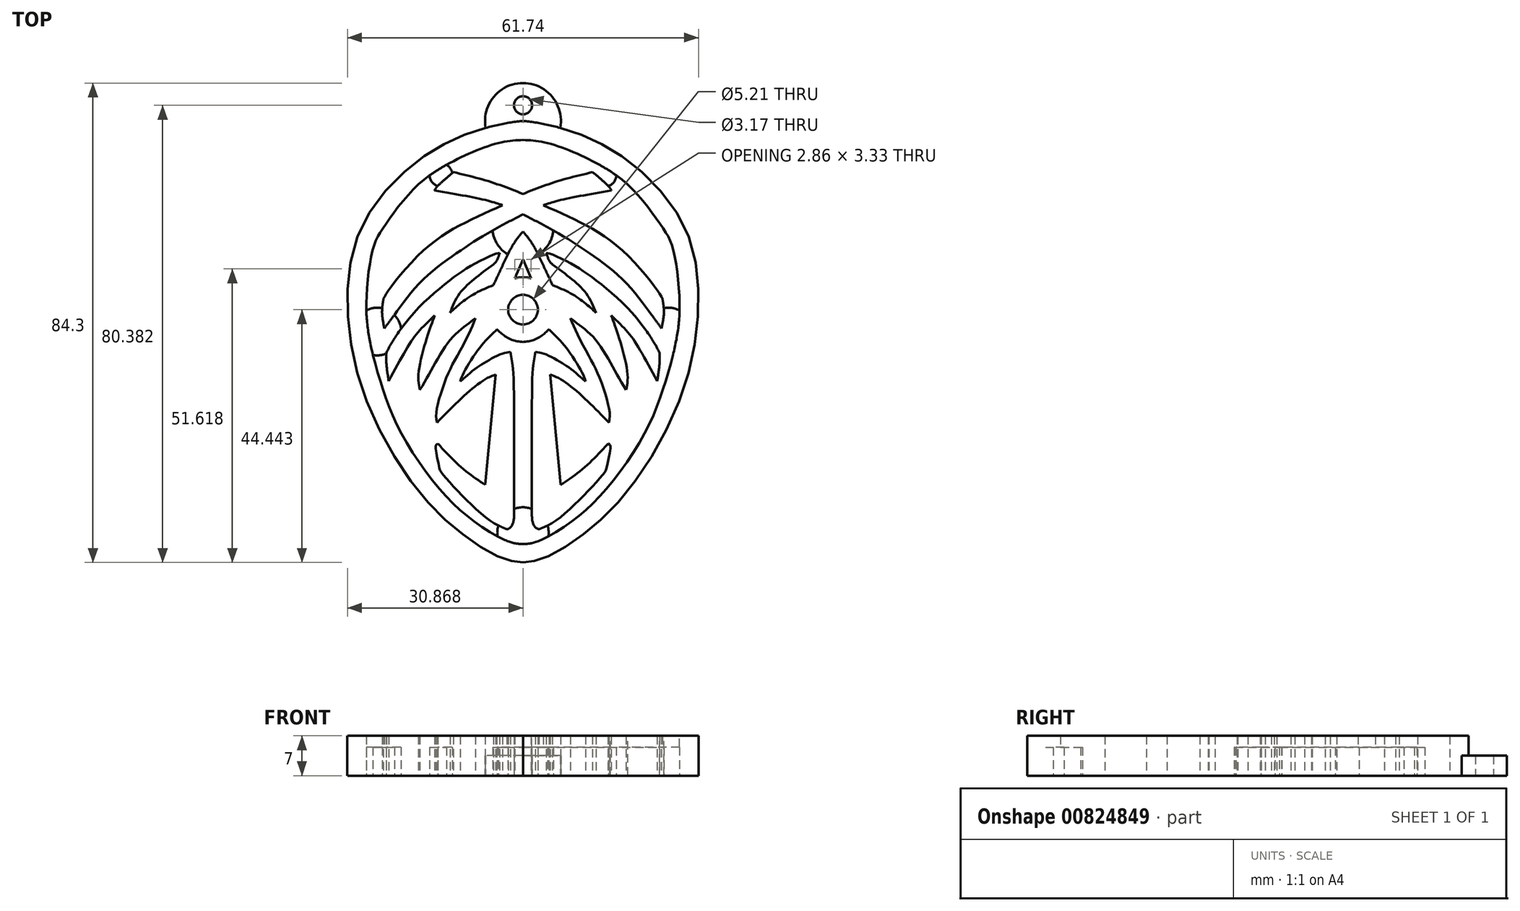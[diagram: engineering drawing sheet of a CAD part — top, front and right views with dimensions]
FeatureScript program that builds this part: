
annotation { "Feature Type Name" : "Feature", "Feature Type Description" : "" }
export const myFeature = defineFeature(function(context is Context, id is Id, definition is map)
    precondition{}
    {
        {
            var Q0;
            Q0=qCreatedBy(makeId("Top.planeOp"),FACE);
            var sketch = newSketch(context, id + "F0", { "sketchPlane" : qUnion([Q0])});
            skFitSpline(sketch, "E0", {"points": [v(2.06, 41.14) * mm, v(-7.13, 39.1) * mm, v(-16.55, 34.05) * mm, v(-26.17, 22.88) * mm, v(-28.79, 8.6) * mm, v(-25.39, -8.21) * mm, v(-16.06, -24.24) * mm, v(-7.51, -32.3) * mm, v(-0.9, -36) * mm, v(2.06, -36.48) * mm], "startDerivative": vector(-78.29, -6.12) * mm, "endDerivative": vector(47.66, -2.85) * mm});
            skFitSpline(sketch, "E1", {"points": [v(2.06, 28.32) * mm, v(-3.58, 30.4) * mm, v(-10.19, 32.15) * mm], "startDerivative": vector(-11.37, 4.54) * mm, "endDerivative": vector(-13.1, 3.15) * mm});
            skFitSpline(sketch, "E2", {"points": [v(-10.19, 32.15) * mm, v(-13.05, 29.58) * mm, v(-13.49, 28.95) * mm], "startDerivative": vector(-5.09, -4.3) * mm, "endDerivative": vector(-1, -1.79) * mm});
            skFitSpline(sketch, "E3", {"points": [v(-13.49, 28.95) * mm, v(-4.21, 27.15) * mm, v(-1.54, 26.32) * mm], "startDerivative": vector(16.5, -2.91) * mm, "endDerivative": vector(6.4, -2.27) * mm});
            skFitSpline(sketch, "E4", {"points": [v(-1.54, 26.32) * mm, v(-8.3, 23.17) * mm, v(-15.34, 18.46) * mm, v(-21.55, 11.41) * mm, v(-22.48, 9.86) * mm], "startDerivative": vector(-25.05, -11.17) * mm, "endDerivative": vector(-4.8, -9.43) * mm});
            skFitSpline(sketch, "E5", {"points": [v(-22.48, 9.86) * mm, v(-22.72, 7.43) * mm, v(-22.3, 4.66) * mm], "startDerivative": vector(-0.82, -4.95) * mm, "endDerivative": vector(1.13, -5.44) * mm});
            skFitSpline(sketch, "E6", {"points": [v(-22.3, 4.66) * mm, v(-20.26, 7.45) * mm, v(-15.71, 13.05) * mm, v(-9.72, 17.83) * mm, v(-4.78, 21.03) * mm, v(2.06, 24.73) * mm], "startDerivative": vector(11.33, 15.95) * mm, "endDerivative": vector(31.86, 16.48) * mm});
            skFitSpline(sketch, "E7", {"points": [v(2.06, 21.7) * mm, v(0.36, 19.46) * mm, v(-1.63, 15.53) * mm, v(-3.13, 12.28) * mm], "startDerivative": vector(-5.76, -6.78) * mm, "endDerivative": vector(-4.31, -9.3) * mm});
            skFitSpline(sketch, "E8", {"points": [v(-3.13, 12.28) * mm, v(-6.44, 10.77) * mm, v(-9.16, 8.88) * mm, v(-10.76, 7.42) * mm], "startDerivative": vector(-9.2, -3.73) * mm, "endDerivative": vector(-5.23, -5) * mm});
            skFitSpline(sketch, "E9", {"points": [v(-10.76, 7.42) * mm, v(-9.3, 10.48) * mm, v(-6.63, 13.25) * mm, v(-3.13, 15.92) * mm], "startDerivative": vector(3.91, 10.14) * mm, "endDerivative": vector(10.1, 7.4) * mm});
            skFitSpline(sketch, "E10", {"points": [v(-3.13, 15.92) * mm, v(-2.62, 16.47) * mm, v(-2.03, 17.93) * mm], "startDerivative": vector(1.3, 1.11) * mm, "endDerivative": vector(0.93, 2.82) * mm});
            skFitSpline(sketch, "E11", {"points": [v(-2.03, 17.93) * mm, v(-2.73, 17.78) * mm, v(-6.47, 16.02) * mm, v(-10.76, 13.15) * mm, v(-17.39, 7.1) * mm, v(-21.27, 1.72) * mm, v(-21.95, 0.38) * mm], "startDerivative": vector(-7.93, -1.03) * mm, "endDerivative": vector(-5.14, -11.02) * mm});
            skFitSpline(sketch, "E12", {"points": [v(-21.95, 0.38) * mm, v(-21.95, -1.61) * mm, v(-21.54, -4.57) * mm], "startDerivative": vector(-0.17, -4.22) * mm, "endDerivative": vector(0.96, -5.63) * mm});
            skFitSpline(sketch, "E13", {"points": [v(-21.54, -4.57) * mm, v(-18.04, 1.68) * mm, v(-16.01, 4.43) * mm, v(-13.47, 6.94) * mm], "startDerivative": vector(8.9, 16.57) * mm, "endDerivative": vector(8.88, 8.6) * mm});
            skFitSpline(sketch, "E14", {"points": [v(-13.47, 6.94) * mm, v(-14.67, 3.54) * mm, v(-16.32, -3.33) * mm, v(-16.08, -6.15) * mm], "startDerivative": vector(-3.37, -9.67) * mm, "endDerivative": vector(1.91, -8.93) * mm});
            skFitSpline(sketch, "E15", {"points": [v(-16.08, -6.15) * mm, v(-13.47, -1.58) * mm, v(-10.55, 2.85) * mm, v(-7.97, 5.19) * mm, v(-6.3, 6.42) * mm], "startDerivative": vector(9.8, 15.42) * mm, "endDerivative": vector(8.23, 5.62) * mm});
            skFitSpline(sketch, "E16", {"points": [v(-6.3, 6.42) * mm, v(-7.32, 4.02) * mm, v(-9.59, -0.3) * mm, v(-11.13, -3.33) * mm, v(-12.61, -7.52) * mm, v(-13.2, -10.37) * mm, v(-13.06, -11.88) * mm], "startDerivative": vector(-5.75, -14.47) * mm, "endDerivative": vector(2.1, -12.33) * mm});
            skFitSpline(sketch, "E17", {"points": [v(-13.06, -11.88) * mm, v(-8.83, -7.7) * mm, v(-4.85, -4.43) * mm, v(-2.72, -3.43) * mm], "startDerivative": vector(10.58, 10.8) * mm, "endDerivative": vector(8.16, 3.08) * mm});
            skFitSpline(sketch, "E18", {"points": [v(-2.72, -3.43) * mm, v(-4.57, -22.84) * mm], "startDerivative": vector(-1.85, -19.4) * mm, "endDerivative": vector(-1.85, -19.4) * mm});
            skFitSpline(sketch, "E19", {"points": [v(-4.57, -22.84) * mm, v(-8.23, -20.23) * mm, v(-11.78, -16.82) * mm, v(-12.9, -15.55) * mm], "startDerivative": vector(-9.56, 6.23) * mm, "endDerivative": vector(-4.07, 4.76) * mm});
            skFitSpline(sketch, "E20", {"points": [v(-12.9, -15.55) * mm, v(-13.25, -15.84) * mm, v(-13.27, -16.66) * mm, v(-12.62, -19.94) * mm, v(-12.33, -20.6) * mm, v(-10.68, -22.54) * mm, v(-6.92, -26.42) * mm, v(-3.24, -29.44) * mm, v(-0.77, -30.65) * mm], "startDerivative": vector(-7.34, -4.48) * mm, "endDerivative": vector(17.38, -7.14) * mm});
            skFitSpline(sketch, "E21", {"points": [v(-0.77, -30.65) * mm, v(-0.2, -30.38) * mm, v(0.33, -29.48) * mm, v(0.5, -26.64) * mm, v(0.4, -3.43) * mm, v(0.1, -0.85) * mm, v(-0.12, 0.52) * mm], "startDerivative": vector(8.3, 2.39) * mm, "endDerivative": vector(-2.1, 13.39) * mm});
            skFitSpline(sketch, "E22", {"points": [v(-0.12, 0.52) * mm, v(-1.56, 0.25) * mm, v(-4.23, -1.08) * mm, v(-6.47, -2.54) * mm, v(-8.56, -4.31) * mm, v(-8.97, -4.65) * mm], "startDerivative": vector(-7.64, -0.68) * mm, "endDerivative": vector(-3.12, -2.46) * mm});
            skFitSpline(sketch, "E23", {"points": [v(-8.97, -4.65) * mm, v(-8.62, -3.69) * mm, v(-6.12, 0.52) * mm, v(-3.81, 3.22) * mm, v(-2.53, 4.5) * mm], "startDerivative": vector(1.39, 4.98) * mm, "endDerivative": vector(5.83, 5.76) * mm});
            skFitSpline(sketch, "E24", {"points": [v(-2.53, 4.5) * mm, v(-2.02, 4.02) * mm, v(-0.12, 2.74) * mm, v(2.06, 2.28) * mm], "startDerivative": vector(1.9, -1.93) * mm, "endDerivative": vector(5.6, -0.54) * mm});
            skFitSpline(sketch, "E25", {"points": [v(2.06, -33.23) * mm, v(-0.05, -32.96) * mm, v(-6, -29.66) * mm, v(-12.63, -23.54) * mm, v(-19.53, -13.45) * mm, v(-22.8, -5.3) * mm, v(-24.82, 2.22) * mm, v(-25.47, 9.6) * mm, v(-24.24, 18.94) * mm, v(-22.48, 22.38) * mm, v(-17.23, 29.1) * mm, v(-10.15, 34.09) * mm, v(-2.05, 37.32) * mm, v(2.06, 37.8) * mm], "startDerivative": vector(-44.62, 0.2) * mm, "endDerivative": vector(64.41, 2.39) * mm});
            skFitSpline(sketch, "E26", {"points": [v(2.06, 16.8) * mm, v(0.63, 13.47) * mm], "startDerivative": vector(-1.43, -3.33) * mm, "endDerivative": vector(-1.43, -3.33) * mm});
            skFitSpline(sketch, "E27", {"points": [v(0.63, 13.47) * mm, v(1.47, 13.63) * mm, v(2.06, 13.64) * mm], "startDerivative": vector(1.6, 0.35) * mm, "endDerivative": vector(1.24, -0.02) * mm});
            skCircle(sketch, "E28", {"center": v(2.06, 7.96) * mm, "radius": 2.6 * mm});
            skFitSpline(sketch, "E29.MirrorCS", {"points": [v(2.06, -33.23) * mm, v(4.16, -32.96) * mm, v(10.11, -29.66) * mm, v(16.74, -23.54) * mm, v(23.65, -13.45) * mm, v(26.9, -5.3) * mm, v(28.94, 2.22) * mm, v(29.59, 9.6) * mm, v(28.35, 18.94) * mm, v(26.6, 22.38) * mm, v(21.34, 29.1) * mm, v(14.27, 34.09) * mm, v(6.16, 37.32) * mm, v(2.06, 37.8) * mm], "startDerivative": vector(44.62, 0.2) * mm, "endDerivative": vector(-64.41, 2.39) * mm});
            skFitSpline(sketch, "E30.MirrorCS", {"points": [v(2.06, 41.14) * mm, v(11.24, 39.1) * mm, v(20.66, 34.05) * mm, v(30.28, 22.88) * mm, v(32.9, 8.6) * mm, v(29.5, -8.21) * mm, v(20.18, -24.24) * mm, v(11.63, -32.3) * mm, v(5.02, -36) * mm, v(2.06, -36.48) * mm], "startDerivative": vector(78.29, -6.12) * mm, "endDerivative": vector(-47.66, -2.85) * mm});
            skFitSpline(sketch, "E31.MirrorCS", {"points": [v(2.06, 28.32) * mm, v(7.7, 30.4) * mm, v(14.3, 32.15) * mm], "startDerivative": vector(11.37, 4.54) * mm, "endDerivative": vector(13.1, 3.15) * mm});
            skFitSpline(sketch, "E32.MirrorCS", {"points": [v(17.6, 28.95) * mm, v(8.33, 27.15) * mm, v(5.66, 26.32) * mm], "startDerivative": vector(-16.5, -2.91) * mm, "endDerivative": vector(-6.4, -2.27) * mm});
            skFitSpline(sketch, "E33.MirrorCS", {"points": [v(5.66, 26.32) * mm, v(12.4, 23.17) * mm, v(19.45, 18.46) * mm, v(25.67, 11.41) * mm, v(26.6, 9.86) * mm], "startDerivative": vector(25.05, -11.17) * mm, "endDerivative": vector(4.8, -9.43) * mm});
            skFitSpline(sketch, "E34.MirrorCS", {"points": [v(26.42, 4.66) * mm, v(24.38, 7.45) * mm, v(19.83, 13.05) * mm, v(13.84, 17.83) * mm, v(8.9, 21.03) * mm, v(2.06, 24.73) * mm], "startDerivative": vector(-11.33, 15.95) * mm, "endDerivative": vector(-31.86, 16.48) * mm});
            skFitSpline(sketch, "E35.MirrorCS", {"points": [v(6.14, 17.93) * mm, v(6.85, 17.78) * mm, v(10.59, 16.02) * mm, v(14.87, 13.15) * mm, v(21.5, 7.1) * mm, v(25.38, 1.72) * mm, v(26.07, 0.38) * mm], "startDerivative": vector(7.93, -1.03) * mm, "endDerivative": vector(5.14, -11.02) * mm});
            skFitSpline(sketch, "E36.MirrorCS", {"points": [v(2.06, 21.7) * mm, v(3.75, 19.46) * mm, v(5.74, 15.53) * mm, v(7.25, 12.28) * mm], "startDerivative": vector(5.76, -6.78) * mm, "endDerivative": vector(4.31, -9.3) * mm});
            skFitSpline(sketch, "E37.MirrorCS", {"points": [v(14.87, 7.42) * mm, v(13.42, 10.48) * mm, v(10.75, 13.25) * mm, v(7.25, 15.92) * mm], "startDerivative": vector(-3.91, 10.14) * mm, "endDerivative": vector(-10.1, 7.4) * mm});
            skFitSpline(sketch, "E38.MirrorCS", {"points": [v(25.66, -4.57) * mm, v(22.15, 1.68) * mm, v(20.13, 4.43) * mm, v(17.59, 6.94) * mm], "startDerivative": vector(-8.9, 16.57) * mm, "endDerivative": vector(-8.88, 8.6) * mm});
            skFitSpline(sketch, "E39.MirrorCS", {"points": [v(26.07, 0.38) * mm, v(26.07, -1.61) * mm, v(25.66, -4.57) * mm], "startDerivative": vector(0.17, -4.22) * mm, "endDerivative": vector(-0.96, -5.63) * mm});
            skFitSpline(sketch, "E40.MirrorCS", {"points": [v(26.6, 9.86) * mm, v(26.83, 7.43) * mm, v(26.42, 4.66) * mm], "startDerivative": vector(0.82, -4.95) * mm, "endDerivative": vector(-1.13, -5.44) * mm});
            skFitSpline(sketch, "E41.MirrorCS", {"points": [v(10.4, 6.42) * mm, v(11.44, 4.02) * mm, v(13.7, -0.3) * mm, v(15.25, -3.33) * mm, v(16.73, -7.52) * mm, v(17.31, -10.37) * mm, v(17.17, -11.88) * mm], "startDerivative": vector(5.75, -14.47) * mm, "endDerivative": vector(-2.1, -12.33) * mm});
            skFitSpline(sketch, "E42.MirrorCS", {"points": [v(20.2, -6.15) * mm, v(17.59, -1.58) * mm, v(14.67, 2.85) * mm, v(12.09, 5.19) * mm, v(10.4, 6.42) * mm], "startDerivative": vector(-9.8, 15.42) * mm, "endDerivative": vector(-8.23, 5.62) * mm});
            skFitSpline(sketch, "E43.MirrorCS", {"points": [v(17.59, 6.94) * mm, v(18.79, 3.54) * mm, v(20.44, -3.33) * mm, v(20.2, -6.15) * mm], "startDerivative": vector(3.37, -9.67) * mm, "endDerivative": vector(-1.91, -8.93) * mm});
            skFitSpline(sketch, "E44.MirrorCS", {"points": [v(17.17, -11.88) * mm, v(12.95, -7.7) * mm, v(8.96, -4.43) * mm, v(6.83, -3.43) * mm], "startDerivative": vector(-10.58, 10.8) * mm, "endDerivative": vector(-8.16, 3.08) * mm});
            skFitSpline(sketch, "E45.MirrorCS", {"points": [v(4.24, 0.52) * mm, v(5.68, 0.25) * mm, v(8.35, -1.08) * mm, v(10.58, -2.54) * mm, v(12.67, -4.31) * mm, v(13.09, -4.65) * mm], "startDerivative": vector(7.64, -0.68) * mm, "endDerivative": vector(3.12, -2.46) * mm});
            skFitSpline(sketch, "E46.MirrorCS", {"points": [v(13.09, -4.65) * mm, v(12.74, -3.69) * mm, v(10.24, 0.52) * mm, v(7.93, 3.22) * mm, v(6.64, 4.5) * mm], "startDerivative": vector(-1.39, 4.98) * mm, "endDerivative": vector(-5.83, 5.76) * mm});
            skFitSpline(sketch, "E47.MirrorCS", {"points": [v(6.64, 4.5) * mm, v(6.13, 4.02) * mm, v(4.24, 2.74) * mm, v(2.06, 2.28) * mm], "startDerivative": vector(-1.9, -1.93) * mm, "endDerivative": vector(-5.6, -0.54) * mm});
            skFitSpline(sketch, "E48.MirrorCS", {"points": [v(4.89, -30.65) * mm, v(4.32, -30.38) * mm, v(3.79, -29.48) * mm, v(3.62, -26.64) * mm, v(3.72, -3.43) * mm, v(4.01, -0.85) * mm, v(4.24, 0.52) * mm], "startDerivative": vector(-8.3, 2.39) * mm, "endDerivative": vector(2.1, 13.39) * mm});
            skFitSpline(sketch, "E49.MirrorCS", {"points": [v(6.83, -3.43) * mm, v(8.69, -22.84) * mm], "startDerivative": vector(1.85, -19.4) * mm, "endDerivative": vector(1.85, -19.4) * mm});
            skFitSpline(sketch, "E50.MirrorCS", {"points": [v(17.02, -15.55) * mm, v(17.37, -15.84) * mm, v(17.39, -16.66) * mm, v(16.73, -19.94) * mm, v(16.45, -20.6) * mm, v(14.8, -22.54) * mm, v(11.04, -26.42) * mm, v(7.36, -29.44) * mm, v(4.89, -30.65) * mm], "startDerivative": vector(7.34, -4.48) * mm, "endDerivative": vector(-17.38, -7.14) * mm});
            skFitSpline(sketch, "E51.MirrorCS", {"points": [v(8.69, -22.84) * mm, v(12.34, -20.23) * mm, v(15.9, -16.82) * mm, v(17.02, -15.55) * mm], "startDerivative": vector(9.56, 6.23) * mm, "endDerivative": vector(4.07, 4.76) * mm});
            skFitSpline(sketch, "E52.MirrorCS", {"points": [v(2.06, 16.8) * mm, v(3.49, 13.47) * mm], "startDerivative": vector(1.43, -3.33) * mm, "endDerivative": vector(1.43, -3.33) * mm});
            skFitSpline(sketch, "E53.MirrorCS", {"points": [v(3.49, 13.47) * mm, v(2.64, 13.63) * mm, v(2.06, 13.64) * mm], "startDerivative": vector(-1.6, 0.35) * mm, "endDerivative": vector(-1.24, -0.02) * mm});
            skFitSpline(sketch, "E54.MirrorCS", {"points": [v(14.3, 32.15) * mm, v(17.17, 29.58) * mm, v(17.6, 28.95) * mm], "startDerivative": vector(5.09, -4.3) * mm, "endDerivative": vector(1, -1.79) * mm});
            skFitSpline(sketch, "E55.MirrorCS", {"points": [v(7.25, 15.92) * mm, v(6.74, 16.47) * mm, v(6.14, 17.93) * mm], "startDerivative": vector(-1.3, 1.11) * mm, "endDerivative": vector(-0.93, 2.82) * mm});
            skFitSpline(sketch, "E56.MirrorCS", {"points": [v(7.25, 12.28) * mm, v(10.55, 10.77) * mm, v(13.27, 8.88) * mm, v(14.87, 7.42) * mm], "startDerivative": vector(9.2, -3.73) * mm, "endDerivative": vector(5.23, -5) * mm});
            skArc(sketch, "E57", {"start": v(8.62, 39.91) * mm, "mid": v(2.06, 47.82) * mm, "end": v(-4.5, 39.91) * mm});
            skCircle(sketch, "E58", {"center": v(2.06, 43.9) * mm, "radius": 1.59 * mm});
            skArc(sketch, "E59", {"start": v(-3.28, 21.89) * mm, "mid": v(-2.45, 19.47) * mm, "end": v(-0.6, 17.7) * mm});
            skArc(sketch, "E60.trimOffspring", {"start": v(4.71, 17.7) * mm, "mid": v(6.57, 19.47) * mm, "end": v(7.4, 21.89) * mm});
            skArc(sketch, "E61", {"start": v(-2.26, -29.99) * mm, "mid": v(-2.45, -30.94) * mm, "end": v(-2.42, -31.9) * mm});
            skArc(sketch, "E62.trimOffspring", {"start": v(3.62, -27.07) * mm, "mid": v(2.06, -26.79) * mm, "end": v(0.5, -27.07) * mm});
            skArc(sketch, "E63.trimOffspring", {"start": v(6.54, -31.9) * mm, "mid": v(6.56, -30.94) * mm, "end": v(6.38, -29.99) * mm});
            skArc(sketch, "E64", {"start": v(-24.31, 0) * mm, "mid": v(-23.12, -0.05) * mm, "end": v(-21.96, 0.24) * mm});
            skArc(sketch, "E65.trimOffspring", {"start": v(-19.39, 4.6) * mm, "mid": v(-19.77, 5.92) * mm, "end": v(-20.56, 7.05) * mm});
            skArc(sketch, "E66.trimOffspring", {"start": v(-22.7, 8.22) * mm, "mid": v(-24.12, 8.27) * mm, "end": v(-25.48, 7.84) * mm});
            skArc(sketch, "E67.MirrorCS", {"start": v(26.81, 8.22) * mm, "mid": v(28.23, 8.27) * mm, "end": v(29.6, 7.84) * mm});
            skArc(sketch, "E68.MirrorCS", {"start": v(23.5, 4.6) * mm, "mid": v(23.88, 5.92) * mm, "end": v(24.67, 7.05) * mm});
            skArc(sketch, "E69.MirrorCS", {"start": v(28.43, 0) * mm, "mid": v(27.23, -0.05) * mm, "end": v(26.07, 0.24) * mm});
            skArc(sketch, "E70", {"start": v(-14.36, 31.57) * mm, "mid": v(-13.94, 30.41) * mm, "end": v(-12.93, 29.71) * mm});
            skArc(sketch, "E71.MirrorC", {"start": v(18.47, 31.57) * mm, "mid": v(18.06, 30.41) * mm, "end": v(17.05, 29.71) * mm});
            skArc(sketch, "E72.trimOffspring", {"start": v(-10.37, 32) * mm, "mid": v(-10.72, 32.83) * mm, "end": v(-11.4, 33.42) * mm});
            skArc(sketch, "E73.trimOffspring", {"start": v(14.48, 32) * mm, "mid": v(14.84, 32.83) * mm, "end": v(15.52, 33.42) * mm});
            skSolve(sketch);
        }
        {
            var Q0;
            {var subQ16=sQuery(id+"F0.wireOp",EDGE,"E1");Q0=makeQuery(id+"F0.imprint","IMPRINT",FACE,{"disambiguationData":[TD([[makeQuery(id+"F0.imprint","IMPRINT",EDGE,{"derivedFrom":subQ16}),1.0]])]});}
            var Q1;
            {var subQ19=sQuery(id+"F0.wireOp",EDGE,"E8");Q1=makeQuery(id+"F0.imprint","IMPRINT",FACE,{"disambiguationData":[TD([[makeQuery(id+"F0.imprint","IMPRINT",EDGE,{"derivedFrom":subQ19}),1.0]])]});}
            var Q2;
            {var subQ3=sQuery(id+"F0.wireOp",EDGE,"E30.MirrorCS");var subQ4=sQuery(id+"F0.wireOp",EDGE,"E0");var subQ5=makeQuery(id+"F0.imprint","INTERSECT",VERTEX,{"disambiguationData":[OD(0.0)],"derivedFrom":[subQ4,subQ3]});Q2=makeQuery(id+"F0.imprint","IMPRINT",FACE,{"disambiguationData":[TD([[makeQuery(id+"F0.imprint","IMPRINT",EDGE,{"disambiguationData":[TD([[subQ5,-1.0]])],"derivedFrom":subQ4}),1.0]])]});}
            extrude(context, id + "F1", {"entities" : qUnion([Q0, Q1, Q2]), "depth" : 7 * mm, "offsetDistance" : 25 * mm});
        }
        {
            var Q0;
            {var subQ0=sQuery(id+"F0.wireOp",EDGE,"E70");Q0=makeQuery(id+"F0.imprint","IMPRINT",FACE,{"disambiguationData":[TD([[makeQuery(id+"F0.imprint","IMPRINT",EDGE,{"derivedFrom":subQ0}),1.0]])]});}
            var Q1;
            {var subQ7=sQuery(id+"F0.wireOp",EDGE,"E59");Q1=makeQuery(id+"F0.imprint","IMPRINT",FACE,{"disambiguationData":[TD([[makeQuery(id+"F0.imprint","IMPRINT",EDGE,{"derivedFrom":subQ7}),1.0]])]});}
            var Q2;
            {var subQ0=sQuery(id+"F0.wireOp",EDGE,"E71.MirrorC");Q2=makeQuery(id+"F0.imprint","IMPRINT",FACE,{"disambiguationData":[TD([[makeQuery(id+"F0.imprint","IMPRINT",EDGE,{"derivedFrom":subQ0}),-1.0]])]});}
            var Q3;
            {var subQ8=sQuery(id+"F0.wireOp",EDGE,"E67.MirrorCS");Q3=makeQuery(id+"F0.imprint","IMPRINT",FACE,{"disambiguationData":[TD([[makeQuery(id+"F0.imprint","IMPRINT",EDGE,{"derivedFrom":subQ8}),-1.0]])]});}
            var Q4;
            {var subQ3=sQuery(id+"F0.wireOp",EDGE,"E64");Q4=makeQuery(id+"F0.imprint","IMPRINT",FACE,{"disambiguationData":[TD([[makeQuery(id+"F0.imprint","IMPRINT",EDGE,{"derivedFrom":subQ3}),1.0]])]});}
            var Q5;
            {var subQ3=sQuery(id+"F0.wireOp",EDGE,"E61");Q5=makeQuery(id+"F0.imprint","IMPRINT",FACE,{"disambiguationData":[TD([[makeQuery(id+"F0.imprint","IMPRINT",EDGE,{"derivedFrom":subQ3}),1.0]])]});}
            extrude(context, id + "F2", {"entities" : qUnion([Q0, Q1, Q2, Q3, Q4, Q5]), "operationType" : NewBodyOperationType.ADD, "depth" : 5 * mm, "offsetDistance" : 25 * mm});
        }
        {
            var Q0;
            {var subQ3=sQuery(id+"F0.wireOp",EDGE,"E57");Q0=makeQuery(id+"F0.imprint","IMPRINT",FACE,{"disambiguationData":[TD([[makeQuery(id+"F0.imprint","IMPRINT",EDGE,{"derivedFrom":subQ3}),1.0]])]});}
            extrude(context, id + "F3", {"entities" : qUnion([Q0]), "operationType" : NewBodyOperationType.ADD, "depth" : 3.5 * mm, "offsetDistance" : 25 * mm});
        }
    });
